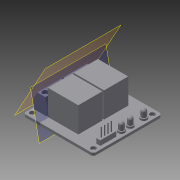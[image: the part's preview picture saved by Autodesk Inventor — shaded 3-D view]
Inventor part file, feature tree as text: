
AUTODESK INVENTOR PART (.ipt)
format: ipt  version: 2016 (Build 200138000, 138)  size: 379,904 bytes
history: native  units: in
note: dims shown in document units (in); Inventor stores cm internally (conversion verified against a paired STEP export)
features: extrude x20, sketch x20, fillet x2, plane x2, chamfer x1
ambient origin geometry x8: Origin, YZ Plane, XZ Plane, XY Plane, X Axis, Y Axis, Z Axis, Center Point
bodies: Solid1 (feature_tree)
feature tree (45):
  extrude  "Extrusion1"  Depth=1.7126in
  extrude  "Extrusion2"  Depth=0.1181in
  sketch  "Sketch3"  dims[d5=0.1181in d6=1.4409in]
  extrude  "Extrusion4"  Depth=1.4409in
  extrude  "Extrusion5"  Depth=0.1142in
  extrude  "Extrusion6"  Depth=0.1181in
  sketch  "Sketch7"  dims[d13=1.4961in d14=0.1024in]
  sketch  "Sketch8"  dims[d15=0.063in d16=0.0in d17=0.5906in d18=0.5906in]
  sketch  "Sketch9"  dims[d19=0.5906in d20=0.5906in]
  extrude  "Extrusion7"  Depth=0.1181in
  extrude  "Extrusion8"  Depth=1.4961in
  extrude  "Extrusion9"  Depth=0.5906in
  fillet  "Fillet1"  Radius=0.5906in
  extrude  "Extrusion10"  Depth=0.5906in
  extrude  "Extrusion11"  Depth=0.2205in
  extrude  "Extrusion12"  Depth=0.3937in
  plane  "Work Plane2"
  extrude  "Extrusion13"  Depth=0.0984in
  plane  "Work Plane3"
  extrude  "Extrusion14"  Depth=0.1181in TaperAngle=0.0deg
  extrude  "Extrusion15"  Depth=0.0236in
  extrude  "Extrusion16"  Depth=0.0236in
  extrude  "Extrusion17"  Depth=0.0512in
  extrude  "Extrusion18"  Depth=0.0827in
  extrude  "Extrusion19"  Depth=0.0512in
  extrude  "Extrusion20"  Depth=0.1575in
  extrude  "Extrusion21"  Depth=0.1575in
  chamfer  "Chamfer1"  Distance=0.315in
  fillet  "Fillet2"  Radius=0.3307in
  sketch  "Sketch1"  dims[d0=1.6772in d1=1.7126in]
  sketch  "Sketch2"  dims[d2=0.063in d3=0.0in d4=0.1181in]
  sketch  "Sketch4"  dims[d7=0.1142in d8=0.1142in]
  sketch  "Sketch5"  dims[d9=0.1142in d10=0.1181in]
  sketch  "Sketch6"  dims[d11=1.4961in d12=0.1181in]
  sketch  "Sketch10"  dims[d21=0.7402in d22=0.2205in]
  sketch  "Sketch11"  dims[d23=0.0394in d26=0.3937in]
  sketch  "Sketch12"  dims[d27=0.0787in d28=0.0984in]
  sketch  "Sketch13"  dims[d29=0.248in d30=0.1181in d31=0.0in]
  sketch  "Sketch14"  dims[d32=0.0236in d33=0.0236in]
  sketch  "Sketch15"  dims[d34=0.0236in d35=0.0236in]
  sketch  "Sketch16"  dims[d36=0.0728in d37=0.0512in]
  sketch  "Sketch17"  dims[d38=0.0827in d39=0.0827in]
  sketch  "Sketch18"  dims[d40=0.0827in d41=0.0512in]
  sketch  "Sketch19"  dims[d42=0.2283in d43=0.0in d44=0.1575in]
  sketch  "Sketch20"  dims[d45=0.1575in d46=0.1575in d48=0.315in d49=0.3307in d50=0.2165in d51=0.1299in d52=0.0472in d53=0.0in d54=0.1181in d55=0.1181in d56=0.1181in d57=0.1693in d58=0.0in d59=0.1693in d60=0.0in d61=0.1693in d62=0.0in d63=0.0591in d64=0.315in d65=0.0276in d66=0.2402in d67=0.5906in d68=0.5906in d69=0.0394in d70=0.2362in d71=0.0in d72=0.1693in d73=0.1969in d74=0.0315in d75=0.1693in d76=0.1693in d77=0.1969in d78=0.0236in d79=0.0236in d80=0.0157in d81=0.0394in d82=0.0in d83=0.0in d84=0.0in d85=0.0591in d86=0.1969in d87=0.1575in d88=0.0in d89=0.0787in d90=0.0in d91=0.0787in d92=0.0in d93=0.1417in d94=0.1417in d95=0.1417in d96=0.0984in d97=0.1969in d98=0.1969in d100=0.0787in d101=0.0in d102=0.1969in d103=0.1575in d104=0.0in d105=0.1575in d106=0.0in d107=0.1575in d108=0.0in d109=0.1417in d110=0.1417in d111=0.1417in d112=0.0984in d113=0.0551in d115=0.0551in d116=0.0984in d117=0.0984in d118=0.0984in d119=0.0787in d120=0.0in d121=0.1693in d122=0.1969in d123=0.1693in d124=0.1969in d125=0.1693in d126=0.1969in d127=0.0157in d128=0.0236in d129=0.0236in d130=0.0394in d131=0.0in d132=0.6181in d133=0.0in d134=0.0394in d135=0.0787in d136=45.0deg d137=0.0079in]
